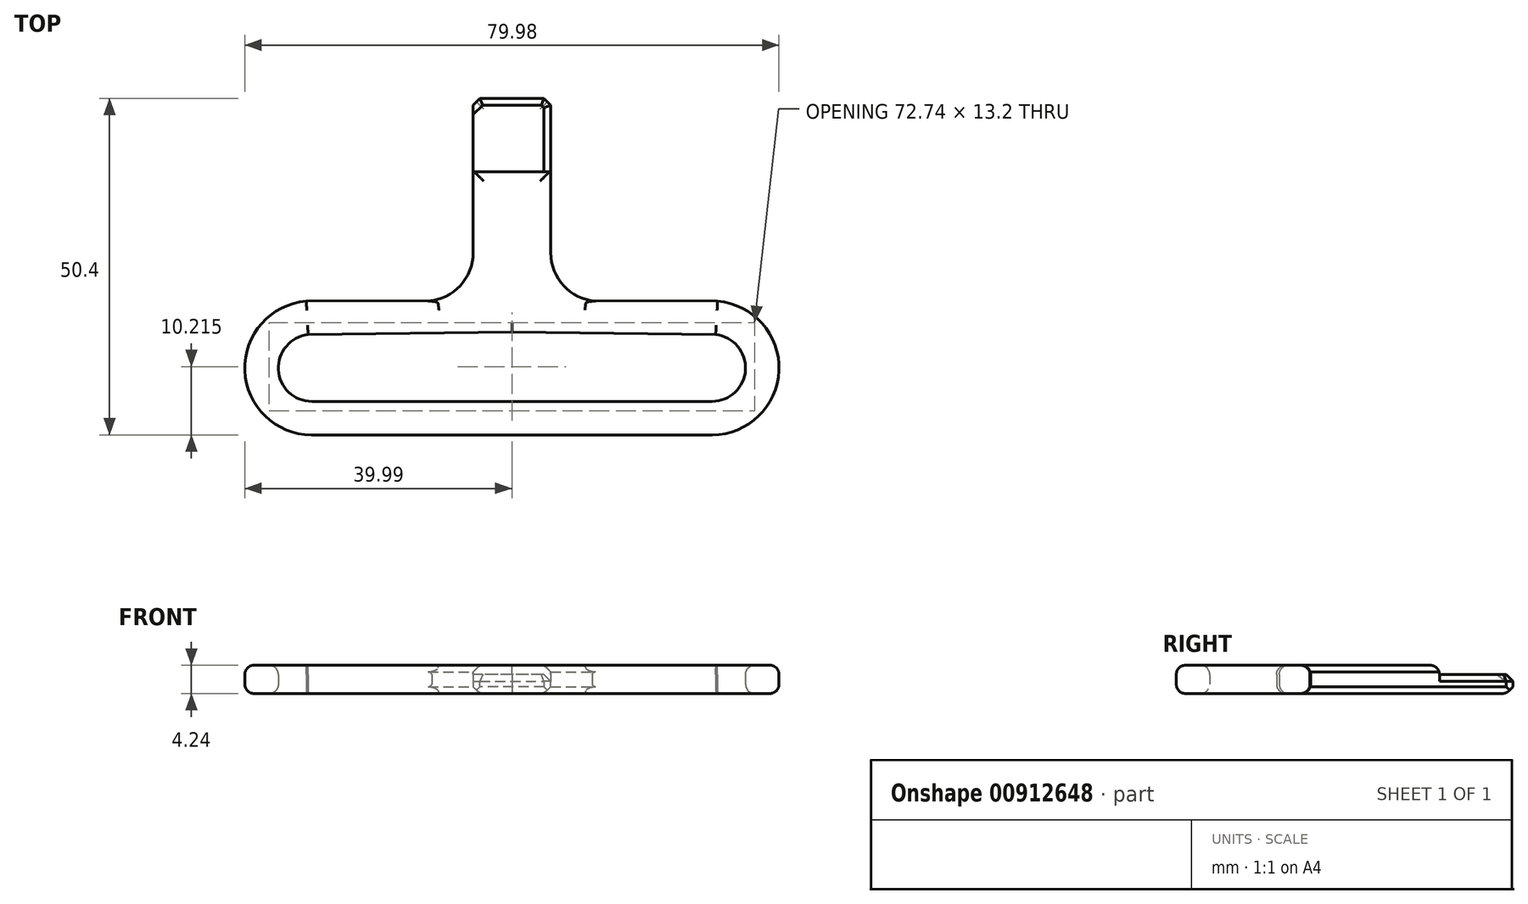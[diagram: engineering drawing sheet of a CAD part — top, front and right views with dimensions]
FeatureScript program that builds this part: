
annotation { "Feature Type Name" : "Feature", "Feature Type Description" : "" }
export const myFeature = defineFeature(function(context is Context, id is Id, definition is map)
    precondition{}
    {
        {
            var Q0;
            Q0=qCreatedBy(makeId("Top.planeOp"),FACE);
            var sketch = newSketch(context, id + "F0", { "sketchPlane" : qUnion([Q0])});
            skLineSegment(sketch, "E0", {"start": v(0, 24.93) * mm, "end": v(5.8, 24.93) * mm});
            skLineSegment(sketch, "E1", {"start": v(5.8, 24.93) * mm, "end": v(5.8, 1.82) * mm});
            skLineSegment(sketch, "E2", {"start": v(30, -25.47) * mm, "end": v(0, -25.47) * mm});
            skArc(sketch, "E3", {"start": v(30, -25.47) * mm, "mid": v(39.98, -15.83) * mm, "end": v(30.78, -5.44) * mm});
            skPoint(sketch, "E4.orphan", {"position": v(5.8, -5) * mm});
            skPoint(sketch, "E5.MirrorCS.end.orphan", {"position": v(0, -25.47) * mm});
            skLineSegment(sketch, "E6", {"start": v(29.96, -20.45) * mm, "end": v(0, -20.45) * mm});
            skArc(sketch, "E7", {"start": v(29.96, -20.45) * mm, "mid": v(34.97, -15.71) * mm, "end": v(30.5, -10.46) * mm});
            skArc(sketch, "E8", {"start": v(5.8, 1.82) * mm, "mid": v(7.56, -2.92) * mm, "end": v(12, -5.37) * mm});
            skLineSegment(sketch, "E9", {"start": v(0, -10.06) * mm, "end": v(30.5, -10.46) * mm});
            skLineSegment(sketch, "E10", {"start": v(30.78, -5.44) * mm, "end": v(12, -5.37) * mm});
            skLineSegment(sketch, "E11.MirrorCS", {"start": v(-30, -25.47) * mm, "end": v(0, -25.47) * mm});
            skLineSegment(sketch, "E12.MirrorCS", {"start": v(0, -10.06) * mm, "end": v(-30.5, -10.46) * mm});
            skLineSegment(sketch, "E13.MirrorCS", {"start": v(-30.78, -5.44) * mm, "end": v(-12, -5.37) * mm});
            skArc(sketch, "E14.MirrorCS", {"start": v(-29.96, -20.45) * mm, "mid": v(-34.97, -15.71) * mm, "end": v(-30.5, -10.46) * mm});
            skArc(sketch, "E15.MirrorCS", {"start": v(-5.8, 1.82) * mm, "mid": v(-7.56, -2.92) * mm, "end": v(-12, -5.37) * mm});
            skLineSegment(sketch, "E16.MirrorCS", {"start": v(0, 24.93) * mm, "end": v(-5.8, 24.93) * mm});
            skLineSegment(sketch, "E17.MirrorCS", {"start": v(-29.96, -20.45) * mm, "end": v(0, -20.45) * mm});
            skLineSegment(sketch, "E18.MirrorCS", {"start": v(-5.8, 24.93) * mm, "end": v(-5.8, 1.82) * mm});
            skArc(sketch, "E19.MirrorCS", {"start": v(-30, -25.47) * mm, "mid": v(-39.98, -15.83) * mm, "end": v(-30.78, -5.44) * mm});
            skPoint(sketch, "E20.MirrorP", {"position": v(-5.8, -5) * mm});
            skSolve(sketch);
        }
        {
            var Q0;
            Q0 = qSketchRegion(id + "F0", true);
            extrude(context, id + "F1", {"entities" : qUnion([Q0]), "depth" : 4.24 * mm, "offsetDistance" : 25 * mm});
        }
        {
            var Q0;
            Q0=makeQuery(id+"F1.opExtrude","CAP_EDGE",EDGE,{"disambiguationData":[OSD([sQuery(id+"F0.wireOp",EDGE,"E16.MirrorCS")])],"isStart":false});
            var Q1;
            Q1=makeQuery(id+"F1.opExtrude","SWEPT_FACE",FACE,{"disambiguationData":[OSD([sQuery(id+"F0.wireOp",EDGE,"E16.MirrorCS")])]});
            var Q2;
            Q2=makeQuery(id+"F1.opExtrude","SWEPT_FACE",FACE,{"disambiguationData":[OSD([sQuery(id+"F0.wireOp",EDGE,"E0")])]});
            chamfer(context, id + "F2", {"entities" : qUnion([Q0, Q1, Q2]), "width" : 1 * mm, "tangentPropagation" : true});
        }
        {
            var Q0;
            Q0=makeQuery(id+"F1.opExtrude","CAP_EDGE",EDGE,{"disambiguationData":[OSD([sQuery(id+"F0.wireOp",EDGE,"E1")])],"isStart":false});
            var Q1;
            Q1=makeQuery(id+"F1.opExtrude","CAP_EDGE",EDGE,{"disambiguationData":[OSD([sQuery(id+"F0.wireOp",EDGE,"E18.MirrorCS")])],"isStart":false});
            var Q2;
            Q2=makeQuery(id+"F1.opExtrude","CAP_EDGE",EDGE,{"disambiguationData":[OSD([sQuery(id+"F0.wireOp",EDGE,"E1")])],"isStart":true});
            var Q3;
            Q3=makeQuery(id+"F1.opExtrude","CAP_EDGE",EDGE,{"disambiguationData":[OSD([sQuery(id+"F0.wireOp",EDGE,"E18.MirrorCS")])],"isStart":true});
            var Q4;
            Q4=makeQuery(id+"F1.opExtrude","CAP_EDGE",EDGE,{"disambiguationData":[OSD([sQuery(id+"F0.wireOp",EDGE,"68d6ee99-1adf-4471-9997-b07b68b0e8cc6.MirrorCS")])],"isStart":true});
            var Q5;
            Q5=makeQuery(id+"F1.opExtrude","CAP_EDGE",EDGE,{"disambiguationData":[OSD([sQuery(id+"F0.wireOp",EDGE,"68d6ee99-1adf-4471-9997-b07b68b0e8cc6.MirrorCS")])],"isStart":false});
            var Q6;
            Q6=makeQuery(id+"F1.opExtrude","CAP_EDGE",EDGE,{"disambiguationData":[OSD([sQuery(id+"F0.wireOp",EDGE,"5Pfn04oZ-tAq5-uVXl-RzR6-5eQ0uUHoxjpo")])],"isStart":false});
            var Q7;
            Q7=makeQuery(id+"F1.opExtrude","CAP_EDGE",EDGE,{"disambiguationData":[OSD([sQuery(id+"F0.wireOp",EDGE,"5Pfn04oZ-tAq5-uVXl-RzR6-5eQ0uUHoxjpo")])],"isStart":true});
            chamfer(context, id + "F3", {"entities" : qUnion([Q0, Q1, Q2, Q3, Q4, Q5, Q6, Q7]), "width" : 1 * mm, "tangentPropagation" : true});
        }
        {
            var Q0;
            Q0=makeQuery(id+"F1.opExtrude","SWEPT_FACE",FACE,{"disambiguationData":[OSD([sQuery(id+"F0.wireOp",EDGE,"E18.MirrorCS")])]});
            var sketch = newSketch(context, id + "F4", { "sketchPlane" : qUnion([Q0])});
            skLineSegment(sketch, "E21.bottom", {"start": v(-25.24, 2.85) * mm, "end": v(-13.93, 2.85) * mm});
            skLineSegment(sketch, "E21.top", {"start": v(-25.24, 5.1) * mm, "end": v(-13.93, 5.1) * mm});
            skLineSegment(sketch, "E21.left", {"start": v(-25.24, 2.85) * mm, "end": v(-25.24, 5.1) * mm});
            skLineSegment(sketch, "E21.right", {"start": v(-13.93, 2.85) * mm, "end": v(-13.93, 5.1) * mm});
            skSolve(sketch);
        }
        {
            var Q0;
            Q0 = qSketchRegion(id + "F4", true);
            extrude(context, id + "F5", {"entities" : qUnion([Q0]), "operationType" : NewBodyOperationType.REMOVE, "oppositeDirection" : true, "depth" : 25 * mm, "offsetDistance" : 25 * mm});
        }
        {
            var Q0;
            Q0=makeQuery(id+"F5.boolean.opBoolean","INTERSECT",EDGE,{"derivedFrom":[makeQuery(id+"F1.opExtrude","SWEPT_FACE",FACE,{"disambiguationData":[OSD([sQuery(id+"F0.wireOp",EDGE,"5Pfn04oZ-tAq5-uVXl-RzR6-5eQ0uUHoxjpo")])]}),makeQuery(id+"F5.opExtrude","SWEPT_FACE",FACE,{"disambiguationData":[OSD([sQuery(id+"F4.wireOp",EDGE,"E21.bottom")])]})]});
            var Q1;
            Q1=makeQuery(id+"F5.boolean.opBoolean","INTERSECT",EDGE,{"derivedFrom":[makeQuery(id+"F1.opExtrude","SWEPT_FACE",FACE,{"disambiguationData":[OSD([sQuery(id+"F0.wireOp",EDGE,"E1")])]}),makeQuery(id+"F5.opExtrude","SWEPT_FACE",FACE,{"disambiguationData":[OSD([sQuery(id+"F4.wireOp",EDGE,"E21.bottom")])]})]});
            var Q2;
            Q2=makeQuery(id+"F5.boolean.opBoolean","INTERSECT",EDGE,{"derivedFrom":[makeQuery(id+"F1.opExtrude","SWEPT_FACE",FACE,{"disambiguationData":[OSD([sQuery(id+"F0.wireOp",EDGE,"68d6ee99-1adf-4471-9997-b07b68b0e8cc6.MirrorCS")])]}),makeQuery(id+"F5.opExtrude","SWEPT_FACE",FACE,{"disambiguationData":[OSD([sQuery(id+"F4.wireOp",EDGE,"E21.bottom")])]})]});
            var Q3;
            Q3=makeQuery(id+"F5.boolean.opBoolean","COPY",EDGE,{"derivedFrom":makeQuery(id+"F5.opExtrude","CAP_EDGE",EDGE,{"disambiguationData":[OSD([sQuery(id+"F4.wireOp",EDGE,"E21.bottom")])],"isStart":true})});
            var Q4;
            Q4=makeQuery(id+"F5.boolean.opBoolean","INTERSECT",EDGE,{"derivedFrom":[makeQuery(id+"F1.opExtrude","SWEPT_FACE",FACE,{"disambiguationData":[OSD([sQuery(id+"F0.wireOp",EDGE,"E16.MirrorCS")])]}),makeQuery(id+"F5.opExtrude","SWEPT_FACE",FACE,{"disambiguationData":[OSD([sQuery(id+"F4.wireOp",EDGE,"E21.bottom")])]})]});
            var Q5;
            Q5=makeQuery(id+"F5.boolean.opBoolean","INTERSECT",EDGE,{"derivedFrom":[makeQuery(id+"F2.opChamfer","BLEND_FACE",FACE,{"disambiguationData":[OSD([sQuery(id+"F0.wireOp",EDGE,"E16.MirrorCS"),sQuery(id+"F0.wireOp",EDGE,"E18.MirrorCS")])]}),makeQuery(id+"F5.opExtrude","SWEPT_FACE",FACE,{"disambiguationData":[OSD([sQuery(id+"F4.wireOp",EDGE,"E21.bottom")])]})]});
            var Q6;
            Q6=makeQuery(id+"F5.boolean.opBoolean","INTERSECT",EDGE,{"derivedFrom":[makeQuery(id+"F2.opChamfer","BLEND_FACE",FACE,{"disambiguationData":[OSD([sQuery(id+"F0.wireOp",EDGE,"68d6ee99-1adf-4471-9997-b07b68b0e8cc6.MirrorCS"),sQuery(id+"F0.wireOp",EDGE,"E16.MirrorCS")])]}),makeQuery(id+"F5.opExtrude","SWEPT_FACE",FACE,{"disambiguationData":[OSD([sQuery(id+"F4.wireOp",EDGE,"E21.bottom")])]})]});
            var Q7;
            Q7=makeQuery(id+"F5.boolean.opBoolean","INTERSECT",EDGE,{"derivedFrom":[makeQuery(id+"F2.opChamfer","BLEND_FACE",FACE,{"disambiguationData":[OSD([sQuery(id+"F0.wireOp",EDGE,"5Pfn04oZ-tAq5-uVXl-RzR6-5eQ0uUHoxjpo"),sQuery(id+"F0.wireOp",EDGE,"E0")])]}),makeQuery(id+"F5.opExtrude","SWEPT_FACE",FACE,{"disambiguationData":[OSD([sQuery(id+"F4.wireOp",EDGE,"E21.bottom")])]})]});
            var Q8;
            Q8=makeQuery(id+"F5.boolean.opBoolean","INTERSECT",EDGE,{"derivedFrom":[makeQuery(id+"F1.opExtrude","SWEPT_FACE",FACE,{"disambiguationData":[OSD([sQuery(id+"F0.wireOp",EDGE,"E0")])]}),makeQuery(id+"F5.opExtrude","SWEPT_FACE",FACE,{"disambiguationData":[OSD([sQuery(id+"F4.wireOp",EDGE,"E21.bottom")])]})]});
            var Q9;
            Q9=makeQuery(id+"F5.boolean.opBoolean","INTERSECT",EDGE,{"derivedFrom":[makeQuery(id+"F2.opChamfer","BLEND_FACE",FACE,{"disambiguationData":[OSD([sQuery(id+"F0.wireOp",EDGE,"E0"),sQuery(id+"F0.wireOp",EDGE,"E1")])]}),makeQuery(id+"F5.opExtrude","SWEPT_FACE",FACE,{"disambiguationData":[OSD([sQuery(id+"F4.wireOp",EDGE,"E21.bottom")])]})]});
            chamfer(context, id + "F6", {"entities" : qUnion([Q0, Q1, Q2, Q3, Q4, Q5, Q6, Q7, Q8, Q9]), "width" : 1 * mm, "tangentPropagation" : true});
        }
        {
            var Q0;
            Q0=makeQuery(id+"F1.opExtrude","CAP_FACE",FACE,{"disambiguationData":[OSD([sQuery(id+"F0.wireOp",EDGE,"E0"),sQuery(id+"F0.wireOp",EDGE,"E1"),sQuery(id+"F0.wireOp",EDGE,"E2"),sQuery(id+"F0.wireOp",EDGE,"E3"),sQuery(id+"F0.wireOp",EDGE,"E6"),sQuery(id+"F0.wireOp",EDGE,"E7"),sQuery(id+"F0.wireOp",EDGE,"E8"),sQuery(id+"F0.wireOp",EDGE,"E9"),sQuery(id+"F0.wireOp",EDGE,"E10"),sQuery(id+"F0.wireOp",EDGE,"E11.MirrorCS"),sQuery(id+"F0.wireOp",EDGE,"E12.MirrorCS"),sQuery(id+"F0.wireOp",EDGE,"E13.MirrorCS"),sQuery(id+"F0.wireOp",EDGE,"E14.MirrorCS"),sQuery(id+"F0.wireOp",EDGE,"E15.MirrorCS"),sQuery(id+"F0.wireOp",EDGE,"E16.MirrorCS"),sQuery(id+"F0.wireOp",EDGE,"E17.MirrorCS"),sQuery(id+"F0.wireOp",EDGE,"E18.MirrorCS"),sQuery(id+"F0.wireOp",EDGE,"E19.MirrorCS")])],"isStart":false});
            var Q1;
            Q1=makeQuery(id+"F1.opExtrude","CAP_FACE",FACE,{"disambiguationData":[OSD([sQuery(id+"F0.wireOp",EDGE,"E0"),sQuery(id+"F0.wireOp",EDGE,"E1"),sQuery(id+"F0.wireOp",EDGE,"E2"),sQuery(id+"F0.wireOp",EDGE,"E3"),sQuery(id+"F0.wireOp",EDGE,"E6"),sQuery(id+"F0.wireOp",EDGE,"E7"),sQuery(id+"F0.wireOp",EDGE,"E8"),sQuery(id+"F0.wireOp",EDGE,"E9"),sQuery(id+"F0.wireOp",EDGE,"E10"),sQuery(id+"F0.wireOp",EDGE,"E11.MirrorCS"),sQuery(id+"F0.wireOp",EDGE,"E12.MirrorCS"),sQuery(id+"F0.wireOp",EDGE,"E13.MirrorCS"),sQuery(id+"F0.wireOp",EDGE,"E14.MirrorCS"),sQuery(id+"F0.wireOp",EDGE,"E15.MirrorCS"),sQuery(id+"F0.wireOp",EDGE,"E16.MirrorCS"),sQuery(id+"F0.wireOp",EDGE,"E17.MirrorCS"),sQuery(id+"F0.wireOp",EDGE,"E18.MirrorCS"),sQuery(id+"F0.wireOp",EDGE,"E19.MirrorCS")])],"isStart":true});
            fillet(context, id + "F7", {"entities" : qUnion([Q0, Q1]), "radius" : 1.4 * mm, "tangentPropagation" : true, "allowEdgeOverflow" : false});
        }
    });
